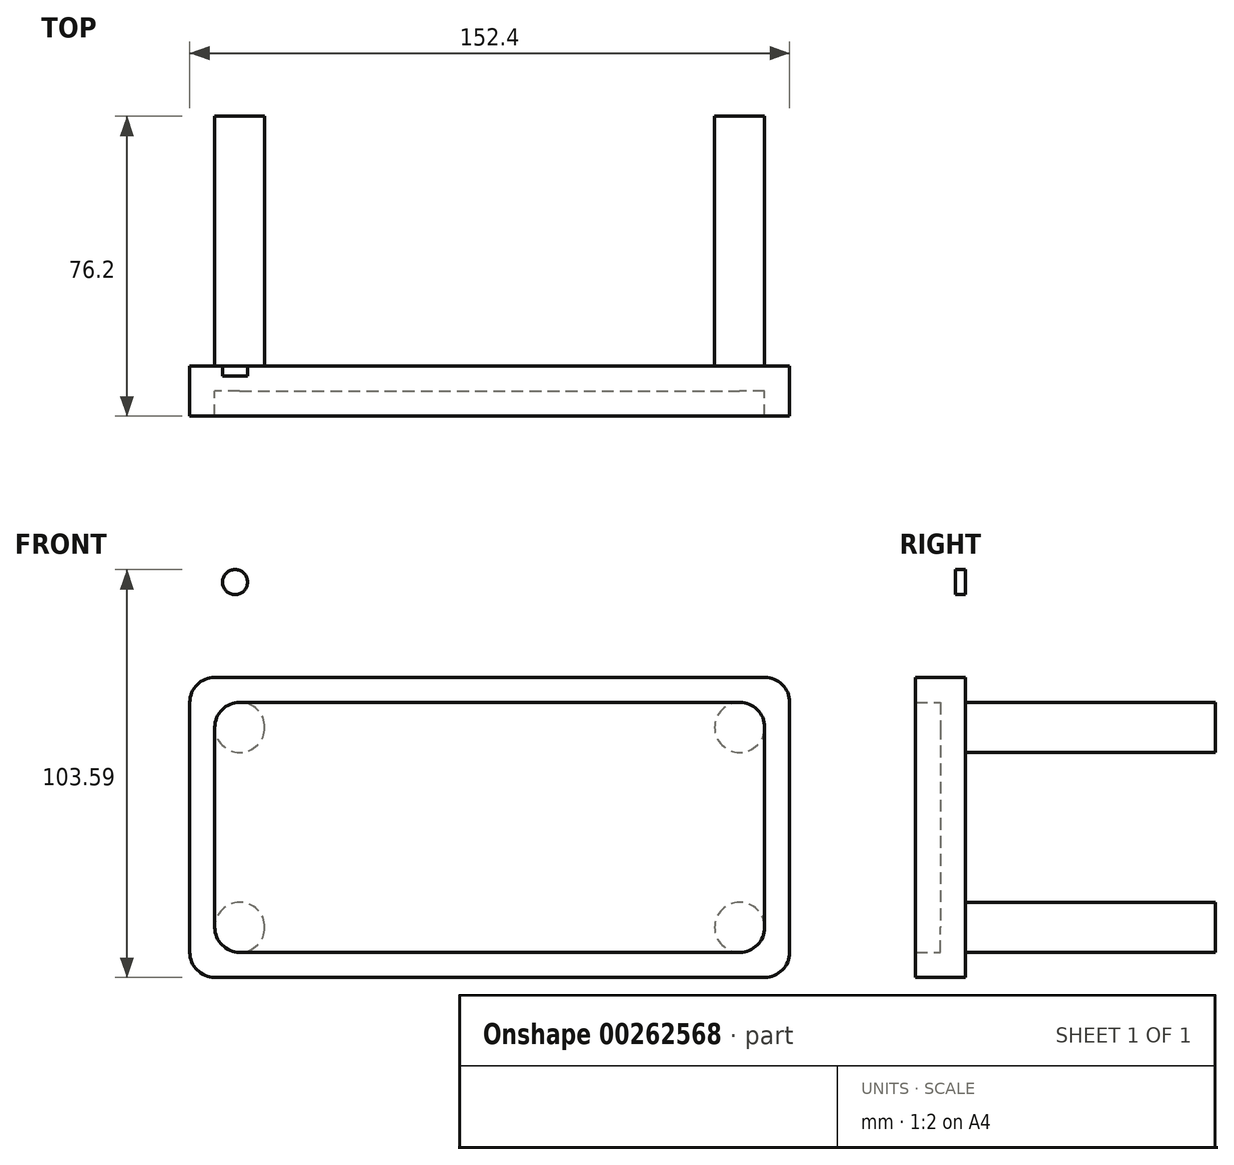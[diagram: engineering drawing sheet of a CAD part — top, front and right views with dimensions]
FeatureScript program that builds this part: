
annotation { "Feature Type Name" : "Feature", "Feature Type Description" : "" }
export const myFeature = defineFeature(function(context is Context, id is Id, definition is map)
    precondition{}
    {
        {
            var Q0;
            Q0=qCreatedBy(makeId("Front.planeOp"),FACE);
            var sketch = newSketch(context, id + "F0", { "sketchPlane" : qUnion([Q0])});
            skLineSegment(sketch, "E0.bottom", {"start": v(-69.85, 38.1) * mm, "end": v(69.85, 38.1) * mm});
            skLineSegment(sketch, "E0.top", {"start": v(-69.85, -38.1) * mm, "end": v(69.85, -38.1) * mm});
            skLineSegment(sketch, "E0.left", {"start": v(-76.2, 31.75) * mm, "end": v(-76.2, -31.75) * mm});
            skLineSegment(sketch, "E0.right", {"start": v(76.2, 31.75) * mm, "end": v(76.2, -31.75) * mm});
            skPoint(sketch, "E0.middle", {"position": v(0, 0) * mm});
            skPoint(sketch, "E1.visualSharp", {"position": v(-76.2, 38.1) * mm});
            skArc(sketch, "E1.filletArc", {"start": v(-69.85, 38.1) * mm, "mid": v(-74.34, 36.24) * mm, "end": v(-76.2, 31.75) * mm});
            skPoint(sketch, "E2.visualSharp", {"position": v(-76.2, -38.1) * mm});
            skArc(sketch, "E2.filletArc", {"start": v(-76.2, -31.75) * mm, "mid": v(-74.34, -36.24) * mm, "end": v(-69.85, -38.1) * mm});
            skPoint(sketch, "E3.visualSharp", {"position": v(76.2, -38.1) * mm});
            skArc(sketch, "E3.filletArc", {"start": v(69.85, -38.1) * mm, "mid": v(74.34, -36.24) * mm, "end": v(76.2, -31.75) * mm});
            skPoint(sketch, "E4.visualSharp", {"position": v(76.2, 38.1) * mm});
            skArc(sketch, "E4.filletArc", {"start": v(76.2, 31.75) * mm, "mid": v(74.34, 36.24) * mm, "end": v(69.85, 38.1) * mm});
            skLineSegment(sketch, "E5.bottom", {"start": v(-63.5, 31.75) * mm, "end": v(63.5, 31.75) * mm});
            skLineSegment(sketch, "E5.top", {"start": v(-63.5, -31.75) * mm, "end": v(63.5, -31.75) * mm});
            skLineSegment(sketch, "E5.left", {"start": v(-69.85, 25.4) * mm, "end": v(-69.85, -25.4) * mm});
            skLineSegment(sketch, "E5.right", {"start": v(69.85, 25.4) * mm, "end": v(69.85, -25.4) * mm});
            skArc(sketch, "E6.filletArc", {"start": v(69.85, 25.4) * mm, "mid": v(68, 29.9) * mm, "end": v(63.5, 31.75) * mm});
            skArc(sketch, "E7.filletArc", {"start": v(63.5, -31.75) * mm, "mid": v(68, -29.9) * mm, "end": v(69.85, -25.4) * mm});
            skArc(sketch, "E8.filletArc", {"start": v(-69.85, -25.4) * mm, "mid": v(-68, -29.9) * mm, "end": v(-63.5, -31.75) * mm});
            skArc(sketch, "E9.filletArc", {"start": v(-63.5, 31.75) * mm, "mid": v(-68, 29.9) * mm, "end": v(-69.85, 25.4) * mm});
            skCircle(sketch, "E10", {"center": v(-63.5, 25.4) * mm, "radius": 6.35 * mm});
            skPoint(sketch, "E10.third.point", {"position": v(-58.38, 21.64) * mm});
            skCircle(sketch, "E11", {"center": v(63.5, 25.4) * mm, "radius": 6.35 * mm});
            skPoint(sketch, "E11.third.point", {"position": v(59.04, 20.88) * mm});
            skCircle(sketch, "E12", {"center": v(63.5, -25.4) * mm, "radius": 6.35 * mm});
            skPoint(sketch, "E12.third.point", {"position": v(59.42, -20.53) * mm});
            skCircle(sketch, "E13", {"center": v(-63.5, -25.4) * mm, "radius": 6.35 * mm});
            skPoint(sketch, "E13.third.point", {"position": v(-57.71, -22.79) * mm});
            skSolve(sketch);
        }
        {
            var Q0;
            Q0=makeQuery(id+"F0.imprint","IMPRINT",FACE,{"disambiguationData":[TD([[makeQuery(id+"F0.imprint","IMPRINT",EDGE,{"derivedFrom":sQuery(id+"F0.wireOp",EDGE,"E0.bottom")}),-1.0]])]});
            extrude(context, id + "F1", {"entities" : qUnion([Q0]), "depth" : 12.7 * mm});
        }
        {
            var Q0;
            {var subQ0=sQuery(id+"F0.wireOp",EDGE,"E10");var subQ1=makeQuery(id+"F0.imprint","INTERSECT",VERTEX,{"derivedFrom":[sQuery(id+"F0.wireOp",EDGE,"E5.bottom"),subQ0]});Q0=makeQuery(id+"F0.imprint","IMPRINT",FACE,{"disambiguationData":[TD([[makeQuery(id+"F0.imprint","IMPRINT",EDGE,{"disambiguationData":[TD([[subQ1,-1.0]])],"derivedFrom":subQ0}),1.0]])]});}
            var Q1;
            {var subQ0=sQuery(id+"F0.wireOp",EDGE,"E13");var subQ1=makeQuery(id+"F0.imprint","INTERSECT",VERTEX,{"derivedFrom":[sQuery(id+"F0.wireOp",EDGE,"E5.top"),subQ0]});Q1=makeQuery(id+"F0.imprint","IMPRINT",FACE,{"disambiguationData":[TD([[makeQuery(id+"F0.imprint","IMPRINT",EDGE,{"disambiguationData":[TD([[subQ1,1.0]])],"derivedFrom":subQ0}),1.0]])]});}
            var Q2;
            {var subQ0=sQuery(id+"F0.wireOp",EDGE,"E12");var subQ1=makeQuery(id+"F0.imprint","INTERSECT",VERTEX,{"derivedFrom":[sQuery(id+"F0.wireOp",EDGE,"E5.top"),subQ0]});Q2=makeQuery(id+"F0.imprint","IMPRINT",FACE,{"disambiguationData":[TD([[makeQuery(id+"F0.imprint","IMPRINT",EDGE,{"disambiguationData":[TD([[subQ1,1.0]])],"derivedFrom":subQ0}),1.0]])]});}
            var Q3;
            {var subQ0=sQuery(id+"F0.wireOp",EDGE,"E11");var subQ1=makeQuery(id+"F0.imprint","INTERSECT",VERTEX,{"derivedFrom":[sQuery(id+"F0.wireOp",EDGE,"E5.bottom"),subQ0]});Q3=makeQuery(id+"F0.imprint","IMPRINT",FACE,{"disambiguationData":[TD([[makeQuery(id+"F0.imprint","IMPRINT",EDGE,{"disambiguationData":[TD([[subQ1,1.0]])],"derivedFrom":subQ0}),1.0]])]});}
            extrude(context, id + "F2", {"entities" : qUnion([Q0, Q1, Q2, Q3]), "oppositeDirection" : true, "depth" : 63.5 * mm});
        }
        {
            var Q0;
            {var subQ3=sQuery(id+"F0.wireOp",EDGE,"E5.bottom");Q0=makeQuery(id+"F0.imprint","IMPRINT",FACE,{"disambiguationData":[TD([[makeQuery(id+"F0.imprint","IMPRINT",EDGE,{"derivedFrom":subQ3}),-1.0]])]});}
            var Q1;
            {var subQ0=sQuery(id+"F0.wireOp",EDGE,"E10");var subQ1=makeQuery(id+"F0.imprint","INTERSECT",VERTEX,{"derivedFrom":[sQuery(id+"F0.wireOp",EDGE,"E5.bottom"),subQ0]});Q1=makeQuery(id+"F0.imprint","IMPRINT",FACE,{"disambiguationData":[TD([[makeQuery(id+"F0.imprint","IMPRINT",EDGE,{"disambiguationData":[TD([[subQ1,-1.0]])],"derivedFrom":subQ0}),1.0]])]});}
            var Q2;
            {var subQ0=sQuery(id+"F0.wireOp",EDGE,"E11");var subQ1=makeQuery(id+"F0.imprint","INTERSECT",VERTEX,{"derivedFrom":[sQuery(id+"F0.wireOp",EDGE,"E5.bottom"),subQ0]});Q2=makeQuery(id+"F0.imprint","IMPRINT",FACE,{"disambiguationData":[TD([[makeQuery(id+"F0.imprint","IMPRINT",EDGE,{"disambiguationData":[TD([[subQ1,1.0]])],"derivedFrom":subQ0}),1.0]])]});}
            var Q3;
            {var subQ0=sQuery(id+"F0.wireOp",EDGE,"E12");var subQ1=makeQuery(id+"F0.imprint","INTERSECT",VERTEX,{"derivedFrom":[sQuery(id+"F0.wireOp",EDGE,"E5.top"),subQ0]});Q3=makeQuery(id+"F0.imprint","IMPRINT",FACE,{"disambiguationData":[TD([[makeQuery(id+"F0.imprint","IMPRINT",EDGE,{"disambiguationData":[TD([[subQ1,1.0]])],"derivedFrom":subQ0}),1.0]])]});}
            var Q4;
            {var subQ0=sQuery(id+"F0.wireOp",EDGE,"E13");var subQ1=makeQuery(id+"F0.imprint","INTERSECT",VERTEX,{"derivedFrom":[sQuery(id+"F0.wireOp",EDGE,"E5.top"),subQ0]});Q4=makeQuery(id+"F0.imprint","IMPRINT",FACE,{"disambiguationData":[TD([[makeQuery(id+"F0.imprint","IMPRINT",EDGE,{"disambiguationData":[TD([[subQ1,1.0]])],"derivedFrom":subQ0}),1.0]])]});}
            extrude(context, id + "F3", {"entities" : qUnion([Q0, Q1, Q2, Q3, Q4]), "operationType" : NewBodyOperationType.ADD, "depth" : 6.35 * mm});
        }
        {
            var Q0;
            Q0=qCreatedBy(makeId("Front.planeOp"),FACE);
            var sketch = newSketch(context, id + "F4", { "sketchPlane" : qUnion([Q0])});
            skCircle(sketch, "E14", {"center": v(-64.7, 62.31) * mm, "radius": 3.18 * mm});
            skSolve(sketch);
        }
        {
            var Q0;
            Q0=makeQuery(id+"F4.imprint","IMPRINT",FACE,{"disambiguationData":[TD([[makeQuery(id+"F4.imprint","IMPRINT",EDGE,{"derivedFrom":sQuery(id+"F4.wireOp",EDGE,"E14")}),1.0]])]});
            extrude(context, id + "F5", {"entities" : qUnion([Q0]), "depth" : 2.54 * mm});
        }
    });
